# Revit family: EN MAN'GO 12
name_source: partatom
category: Equipement spécialisé
units: mm (PartAtom-declared; Revit-internal decimal feet)

## family parameters
Basée sur le plan de construction = Non
Cote de connecteur circulaire = Utiliser le diamètre
Couper avec des vides une fois chargée = Non
Numéro OmniClass = 23.50.00.00
Partagée = Non
Point de calcul de pièce = Non
Titre OmniClass = Conveying Systems & Material Handling
Toujours verticalement = Oui
Type d'élément = Normal

## types (1)
- MAN'GO 12
    Average consumption (L/h) = 1.324
    Average consumption (l/day) = 0 m
    CO2 emissions (g/kWh) = 3.5
    Commentaires du type = Nacelle elevatrice compacte et légère
    Counterweight offset (turret at 90°) = 0.19 m
    Créé par = ATLANCAD
    Elévation par défaut = 0 m
    Engine norm = Stage V
    External turning radius = 4.11 m
    Fabricant = MANITOU
    Floor height (access) = 0.3 m
    Ground clearance = 0.2 m
    Ground clearance at centre of wheelbase = 0.32 m
    I.C. Engine power rating - Power (ch) = 26
    I.C. Engine power rating - Power (kW) = 18.5
    Internal turning radius (over tyres) = 1.71 m
    Jib length = 1.46 m
    Max. lifting height = 11.91 m
    Max. outreach = 6.69 m
    Modèle = MAN'GO 12
    Noise to environment (LwA) = 100
    Number of people (inside) = 2
    Number of people (outside) = 2
    Overall height (stowed) = 4.5 m
    Overall height (transport) = 2.02 m
    Overall lenght (stowed) = 4.5 m
    Overall lenght (transport) = 5.5 m
    Overhang = 4.8 m
    Permissible leveling = 4.00°
    Platform capacity = 230.00 kg
    Platform dimensions (length) = 1.5 m
    Platform dimensions (width) = 0.98 m
    Platform weight = 4150.00 kg
    URL = www.manitou.com
    Wheelbase = 2 m
    Width = 1.8 m
